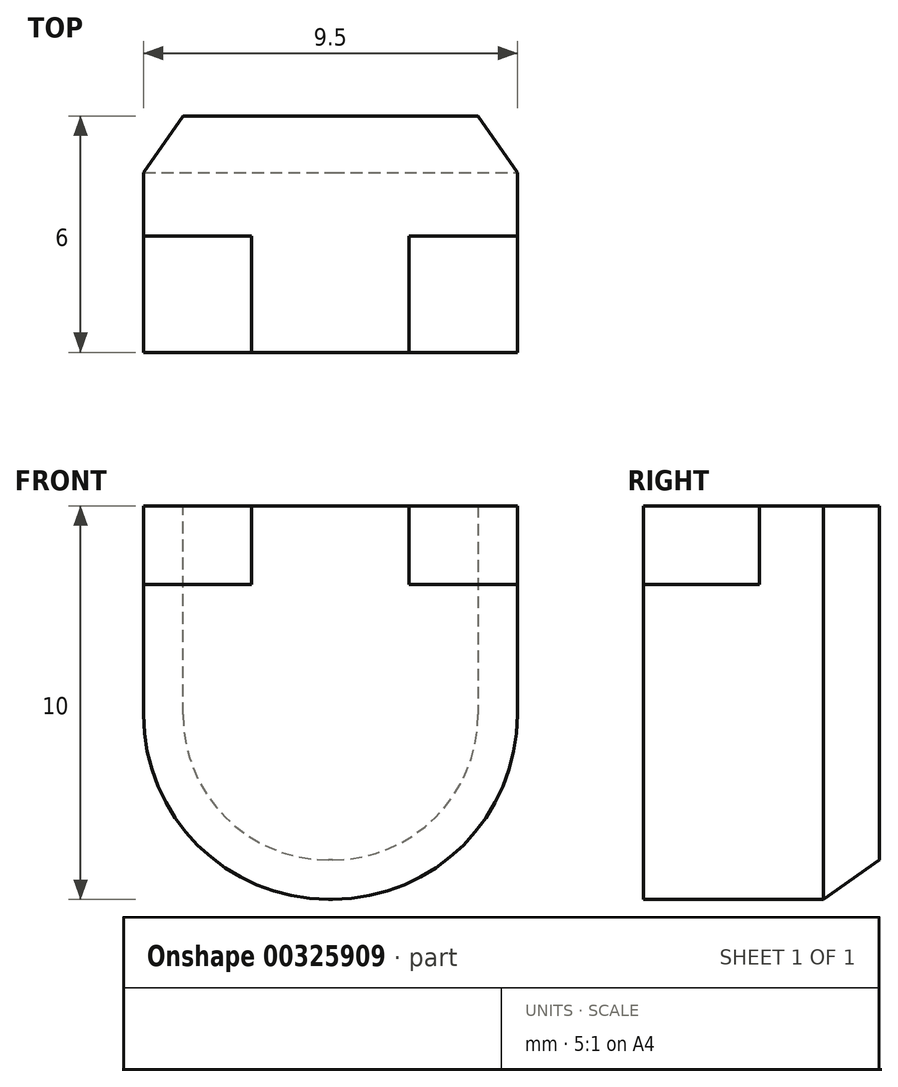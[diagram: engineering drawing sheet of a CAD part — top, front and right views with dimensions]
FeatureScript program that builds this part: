
annotation { "Feature Type Name" : "Feature", "Feature Type Description" : "" }
export const myFeature = defineFeature(function(context is Context, id is Id, definition is map)
    precondition{}
    {
        {
            var Q0;
            Q0=qCreatedBy(makeId("Front.planeOp"),FACE);
            var sketch = newSketch(context, id + "F0", { "sketchPlane" : qUnion([Q0])});
            skLineSegment(sketch, "E0.bottom", {"start": v(4.75, 5) * mm, "end": v(-4.75, 5) * mm});
            skLineSegment(sketch, "E0.top", {"start": v(4.75, -5) * mm, "end": v(-4.75, -5) * mm});
            skLineSegment(sketch, "E0.left", {"start": v(4.75, 5) * mm, "end": v(4.75, -5) * mm});
            skLineSegment(sketch, "E0.right", {"start": v(-4.75, 5) * mm, "end": v(-4.75, -5) * mm});
            skPoint(sketch, "E0.middle", {"position": v(0, 0) * mm});
            skLineSegment(sketch, "E1", {"start": v(0, 5) * mm, "end": v(2, 5) * mm});
            skLineSegment(sketch, "E2", {"start": v(2, 5) * mm, "end": v(-2, 5) * mm});
            skLineSegment(sketch, "E3.bottom", {"start": v(-2, 5) * mm, "end": v(2, 5) * mm});
            skLineSegment(sketch, "E3.top", {"start": v(-2, 3) * mm, "end": v(2, 3) * mm});
            skLineSegment(sketch, "E3.left", {"start": v(-2, 5) * mm, "end": v(-2, 3) * mm});
            skLineSegment(sketch, "E3.right", {"start": v(2, 5) * mm, "end": v(2, 3) * mm});
            skLineSegment(sketch, "E4", {"start": v(-2, 3) * mm, "end": v(-4.75, 3) * mm});
            skLineSegment(sketch, "E5", {"start": v(2, 3) * mm, "end": v(4.75, 3) * mm});
            skSolve(sketch);
        }
        {
            var Q0;
            Q0 = qSketchRegion(id + "F0", true);
            extrude(context, id + "F1", {"entities" : qUnion([Q0]), "oppositeDirection" : true, "depth" : 6 * mm});
        }
        {
            var Q0;
            {var subQ3=sQuery(id+"F0.wireOp",EDGE,"E3.left");Q0=makeQuery(id+"F0.imprint","IMPRINT",FACE,{"disambiguationData":[TD([[makeQuery(id+"F0.imprint","IMPRINT",EDGE,{"derivedFrom":subQ3}),-1.0]])]});}
            var Q1;
            {var subQ3=sQuery(id+"F0.wireOp",EDGE,"E3.right");Q1=makeQuery(id+"F0.imprint","IMPRINT",FACE,{"disambiguationData":[TD([[makeQuery(id+"F0.imprint","IMPRINT",EDGE,{"derivedFrom":subQ3}),1.0]])]});}
            extrude(context, id + "F2", {"entities" : qUnion([Q0, Q1]), "operationType" : NewBodyOperationType.REMOVE, "oppositeDirection" : true, "depth" : 2.95 * mm});
        }
        {
            var Q0;
            Q0=makeQuery(id+"F1.opExtrude","SWEPT_EDGE",EDGE,{"disambiguationData":[OSD([sQuery(id+"F0.wireOp",EDGE,"E0.top"),sQuery(id+"F0.wireOp",EDGE,"E0.right")])]});
            var Q1;
            Q1=makeQuery(id+"F1.opExtrude","SWEPT_EDGE",EDGE,{"disambiguationData":[OSD([sQuery(id+"F0.wireOp",EDGE,"E0.top"),sQuery(id+"F0.wireOp",EDGE,"E0.left")])]});
            fillet(context, id + "F3", {"entities" : qUnion([Q0, Q1]), "radius" : 4.7 * mm, "tangentPropagation" : true, "allowEdgeOverflow" : false});
        }
        {
            var Q0;
            {var subQ0=sQuery(id+"F0.wireOp",EDGE,"E0.left");var subQ1=sQuery(id+"F0.wireOp",EDGE,"E0.top");Q0=makeQuery(id+"F3.opFillet","BLEND_EDGE",EDGE,{"blendedFrom":[makeQuery(id+"F1.opExtrude","SWEPT_EDGE",EDGE,{"disambiguationData":[OSD([subQ1,subQ0])]}),makeQuery(id+"F1.opExtrude","CAP_FACE",FACE,{"disambiguationData":[OSD([sQuery(id+"F0.wireOp",EDGE,"E0.bottom"),subQ1,subQ0,sQuery(id+"F0.wireOp",EDGE,"E0.right"),sQuery(id+"F0.wireOp",EDGE,"E3.bottom")])],"isStart":false})],"blendedInto":[makeQuery(id+"F1.opExtrude","CAP_FACE",FACE,{"disambiguationData":[OSD([sQuery(id+"F0.wireOp",EDGE,"E0.bottom"),subQ1,subQ0,sQuery(id+"F0.wireOp",EDGE,"E0.right"),sQuery(id+"F0.wireOp",EDGE,"E3.bottom")])],"isStart":false})]});}
            var Q1;
            {var subQ0=sQuery(id+"F0.wireOp",EDGE,"E0.right");var subQ1=sQuery(id+"F0.wireOp",EDGE,"E0.top");Q1=makeQuery(id+"F3.opFillet","BLEND_EDGE",EDGE,{"blendedFrom":[makeQuery(id+"F1.opExtrude","SWEPT_EDGE",EDGE,{"disambiguationData":[OSD([subQ1,subQ0])]}),makeQuery(id+"F1.opExtrude","CAP_FACE",FACE,{"disambiguationData":[OSD([sQuery(id+"F0.wireOp",EDGE,"E0.bottom"),subQ1,sQuery(id+"F0.wireOp",EDGE,"E0.left"),subQ0,sQuery(id+"F0.wireOp",EDGE,"E3.bottom")])],"isStart":false})],"blendedInto":[makeQuery(id+"F1.opExtrude","CAP_FACE",FACE,{"disambiguationData":[OSD([sQuery(id+"F0.wireOp",EDGE,"E0.bottom"),subQ1,sQuery(id+"F0.wireOp",EDGE,"E0.left"),subQ0,sQuery(id+"F0.wireOp",EDGE,"E3.bottom")])],"isStart":false})]});}
            var Q2;
            Q2=makeQuery(id+"F1.opExtrude","CAP_EDGE",EDGE,{"disambiguationData":[OSD([sQuery(id+"F0.wireOp",EDGE,"E0.top")])],"isStart":false});
            chamfer(context, id + "F4", {"entities" : qUnion([Q0, Q1, Q2]), "chamferType" : ChamferType.OFFSET_ANGLE, "width" : 1 * mm, "oppositeDirection" : false, "angle" : 55 * degree, "tangentPropagation" : true});
        }
    });
